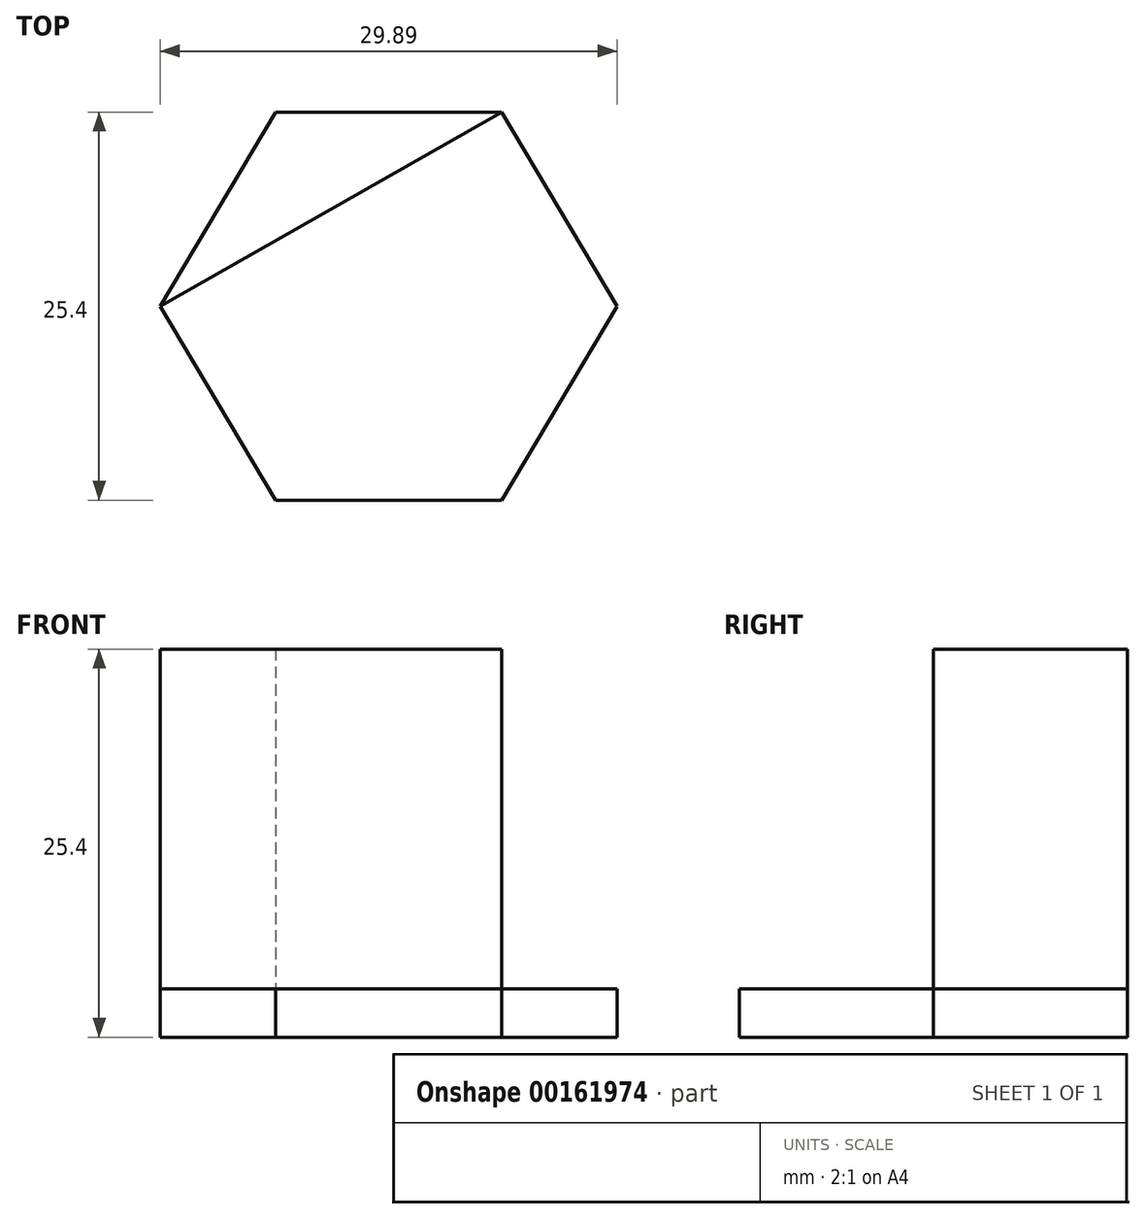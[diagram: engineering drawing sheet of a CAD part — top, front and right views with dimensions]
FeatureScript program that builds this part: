
annotation { "Feature Type Name" : "Feature", "Feature Type Description" : "" }
export const myFeature = defineFeature(function(context is Context, id is Id, definition is map)
    precondition{}
    {
        {
            var Q0;
            Q0=qCreatedBy(makeId("Top.planeOp"),FACE);
            var sketch = newSketch(context, id + "F0", { "sketchPlane" : qUnion([Q0])});
            skLineSegment(sketch, "E0", {"start": v(0, 0) * mm, "end": v(7.56, 12.7) * mm});
            skLineSegment(sketch, "E1", {"start": v(7.56, 12.7) * mm, "end": v(22.34, 12.7) * mm});
            skLineSegment(sketch, "E2", {"start": v(22.34, 12.7) * mm, "end": v(29.9, 0) * mm});
            skLineSegment(sketch, "E3", {"start": v(29.9, 0) * mm, "end": v(22.34, -12.7) * mm});
            skLineSegment(sketch, "E4", {"start": v(22.34, -12.7) * mm, "end": v(7.56, -12.7) * mm});
            skLineSegment(sketch, "E5", {"start": v(7.56, -12.7) * mm, "end": v(0, 0) * mm});
            skSolve(sketch);
        }
        {
            var Q0;
            Q0=makeQuery(id+"F0.imprint","IMPRINT",FACE,{"disambiguationData":[TD([[makeQuery(id+"F0.imprint","IMPRINT",EDGE,{"derivedFrom":sQuery(id+"F0.wireOp",EDGE,"E0")}),-1.0]])]});
            extrude(context, id + "F1", {"entities" : qUnion([Q0]), "depth" : 3.17 * mm});
        }
        {
            var Q0;
            Q0=makeQuery(id+"F1.opExtrude","CAP_FACE",FACE,{"disambiguationData":[OSD([sQuery(id+"F0.wireOp",EDGE,"E0"),sQuery(id+"F0.wireOp",EDGE,"E1"),sQuery(id+"F0.wireOp",EDGE,"E2"),sQuery(id+"F0.wireOp",EDGE,"E3"),sQuery(id+"F0.wireOp",EDGE,"E4"),sQuery(id+"F0.wireOp",EDGE,"E5")])],"isStart":false});
            var sketch = newSketch(context, id + "F2", { "sketchPlane" : qUnion([Q0])});
            skLineSegment(sketch, "E6", {"start": v(0, 0) * mm, "end": v(22.34, 12.7) * mm});
            skSolve(sketch);
        }
        {
            var Q0;
            {var subQ0=sQuery(id+"F2.wireOp",EDGE,"HGEBFMjn-vmWw-1zcE-P0Vb-IEOj8MIbl7Tx");Q0=makeQuery(id+"F2.imprint","IMPRINT",FACE,{"disambiguationData":[TD([[makeQuery(id+"F2.imprint","IMPRINT",EDGE,{"derivedFrom":subQ0}),1.0]])]});}
            var Q1;
            Q1=makeQuery(id+"F2.imprint","IMPRINT",FACE,{"disambiguationData":[TD([[makeQuery(id+"F2.imprint","IMPRINT",EDGE,{"derivedFrom":sQuery(id+"F2.wireOp",EDGE,"E6")}),1.0]])]});
            extrude(context, id + "F3", {"entities" : qUnion([Q0, Q1]), "operationType" : NewBodyOperationType.ADD, "depth" : 22.22 * mm});
        }
    });
